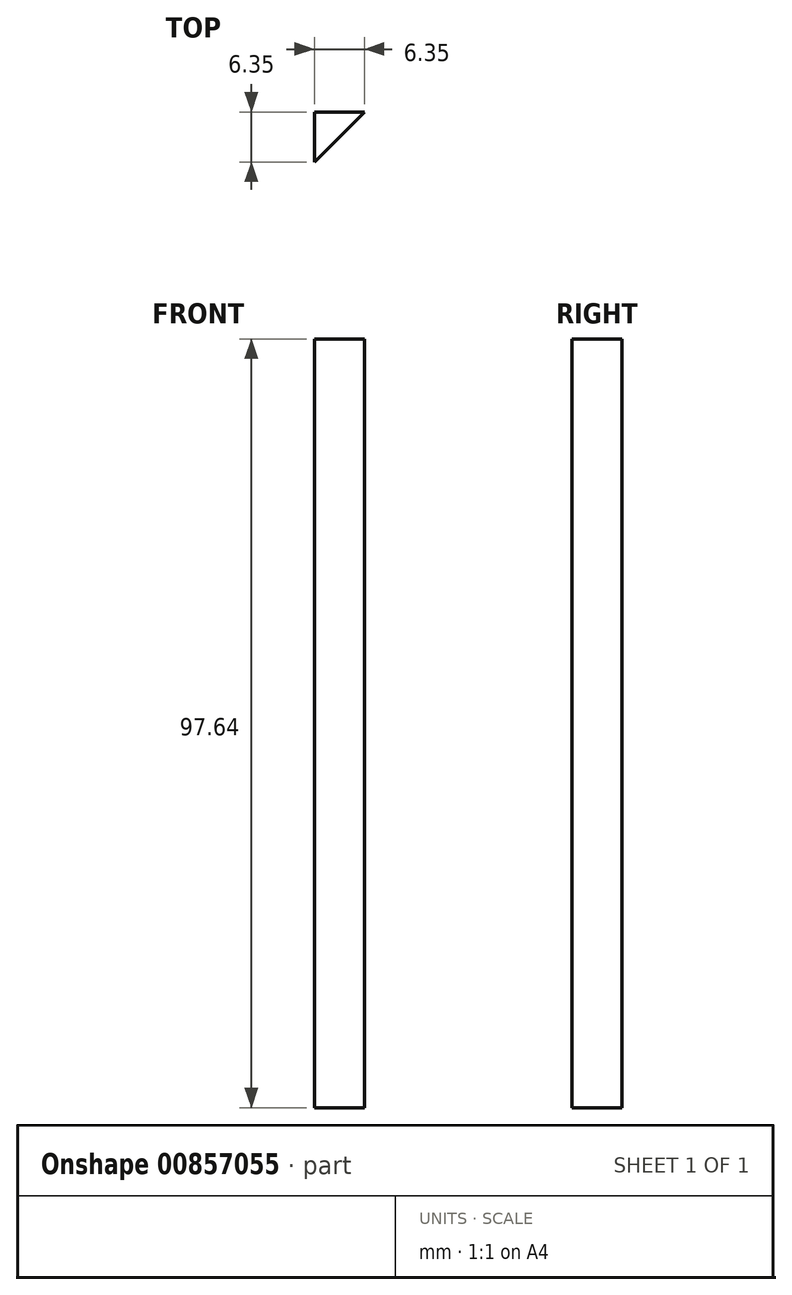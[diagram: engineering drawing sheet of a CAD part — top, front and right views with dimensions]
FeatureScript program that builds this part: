
annotation { "Feature Type Name" : "Feature", "Feature Type Description" : "" }
export const myFeature = defineFeature(function(context is Context, id is Id, definition is map)
    precondition{}
    {
        {
            var Q0;
            Q0=qCreatedBy(makeId("Top.planeOp"),FACE);
            var sketch = newSketch(context, id + "F0", { "sketchPlane" : qUnion([Q0])});
            skLineSegment(sketch, "E0", {"start": v(0, 0) * mm, "end": v(0, -6.35) * mm});
            skLineSegment(sketch, "E1", {"start": v(0, 0) * mm, "end": v(6.35, 0) * mm});
            skLineSegment(sketch, "E2", {"start": v(6.35, 0) * mm, "end": v(0, -6.35) * mm});
            skSolve(sketch);
        }
        {
            var Q0;
            Q0 = qSketchRegion(id + "F0", true);
            extrude(context, id + "F1", {"entities" : qUnion([Q0]), "depth" : 97.63 * mm, "offsetDistance" : 25.4 * mm, "symmetric" : true});
        }
    });
